# Revit family: Distanzmuffe sechskant VA
name_source: partatom
category: HLS-Bauteile
revit_build: Autodesk Revit 2017 (Build: 20190507_1515(x64)
units: mm (PartAtom-declared; Revit-internal decimal feet)

## family parameters
Arbeitsebenenbasiert = Nein
Beim Laden mit Abzugskörper schneiden = Nein
Bemaßung runder Anschluss = Durchmesser verwenden
Gemeinsam genutzt = Ja
Immer vertikal = Nein
Raumberechnungspunkt = Nein
Teiletyp = Normal

## types (8) — shared parameters
Fabrikat = MEFA
Material = Edelstahl
Mengeneinheit = St

## per-type parameters (varying)
| type | Artikelnummer | D | EAN | Gewicht | Gewicht pro Bauteil | Kurztext1 | Kurztext2 | L | Länge | SW | vpe |
| Distanzmuffe sechskant M 8, V2A | 0702830 | 3 mm  [stored 0.00984252 ft] | 4250928416230 | 0.03 kg | 0.03 kg | Distanzmuffe sechskant V2A | Innengew. M8 L= 30 mm | 30 mm  [stored 0.0984252 ft] | 30 mm  [stored 0.0984252 ft] | 7 mm  [stored 0.0229659 ft] | 100 St |
| Distanzmuffe sechskant M10, V2A | 0702835 | 4 mm  [stored 0.0131234 ft] | 4250928416247 | 0.06 kg | 0.06 kg | Distanzmuffe sechskant V2A | Innengew. M10 L= 40 mm | 40 mm  [stored 0.131234 ft] | 40 mm  [stored 0.131234 ft] | 9 mm | 50 St |
| Distanzmuffe sechskant M12, V2A | 0702840 | 5 mm  [stored 0.0164042 ft] | 4250928416254 | 0.07 kg | 0.07 kg | Distanzmuffe sechskant V2A | Innengew. M12 L= 40 mm | 40 mm  [stored 0.131234 ft] | 40 mm  [stored 0.131234 ft] | 9 mm | 50 St |
| Distanzmuffe sechskant M16, V2A | 0702844 | 7 mm  [stored 0.0229659 ft] | 4250928416261 | 0.11 kg | 0.11 kg | Distanzmuffe sechskant V2A | Innengew. M16 L= 40 mm | 40 mm  [stored 0.131234 ft] | 40 mm  [stored 0.131234 ft] | 12 mm  [stored 0.0393701 ft] | 25 St |
| Distanzmuffe sechskant M 8, V4A | 0702880 | 3 mm  [stored 0.00984252 ft] | 4250928416278 | 0.03 kg | 0.03 kg | Distanzmuffe sechskant V4A | Innengew. M8 L= 30 mm | 30 mm  [stored 0.0984252 ft] | 30 mm  [stored 0.0984252 ft] | 7 mm  [stored 0.0229659 ft] | 100 St |
| Distanzmuffe sechskant M10, V4A | 0702883 | 4 mm  [stored 0.0131234 ft] | 4250928416285 | 0.05 kg | 0.05 kg | Distanzmuffe sechskant V4A | Innengew. M10 L= 30 mm | 30 mm  [stored 0.0984252 ft] | 30 mm  [stored 0.0984252 ft] | 9 mm | 50 St |
| Distanzmuffe sechskant M12, V4A | 0702888 | 5 mm  [stored 0.0164042 ft] | 4250928416292 | 0.06 kg | 0.06 kg | Distanzmuffe sechskant V4A | Innengew. M12 L= 30 mm | 30 mm  [stored 0.0984252 ft] | 30 mm  [stored 0.0984252 ft] | 9 mm | 50 St |
| Distanzmuffe sechskant M16, V4A | 0702894 | 7 mm  [stored 0.0229659 ft] | 4250928416308 | 0.11 kg | 0.11 kg | Distanzmuffe sechskant V4A | Innengew. M16 L= 40 mm | 40 mm  [stored 0.131234 ft] | 40 mm  [stored 0.131234 ft] | 12 mm  [stored 0.0393701 ft] | 25 St |

note: [stored X ft] marks values corroborated as IEEE doubles in the binary element streams (Revit-internal decimal feet)

## geometry (parser evidence)
native form markers: Sweep x3
no freeform markers — native parametric forms only
